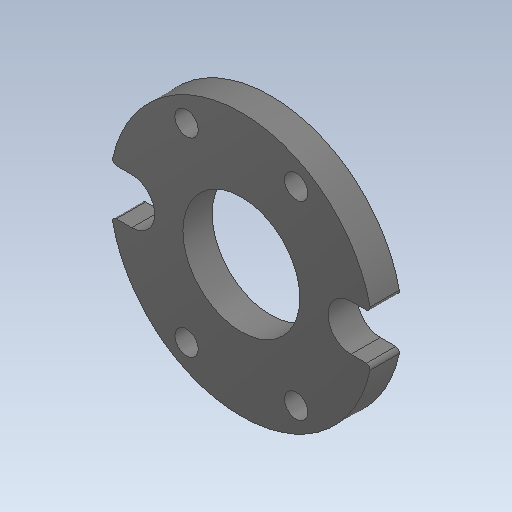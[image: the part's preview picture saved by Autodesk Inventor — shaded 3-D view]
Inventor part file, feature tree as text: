
AUTODESK INVENTOR PART (.ipt)
format: ipt  version: 2020 (Build 240168000, 168)  size: 119,296 bytes
history: native  units: in
note: dims shown in document units (in); Inventor stores cm internally (conversion verified against a paired STEP export)
features: fillet x1
ambient origin geometry x8: Origin, YZ Plane, XZ Plane, XY Plane, X Axis, Y Axis, Z Axis, Center Point
bodies: Solid1 (feature_tree)
feature tree (1):
  fillet  "Fillet1"  [1 undecoded]
note: 1 required parameter value undecoded (feature->parameter linkage not recoverable at this tier; creation-order binding heuristic only, values carry confidence <= 0.55)
